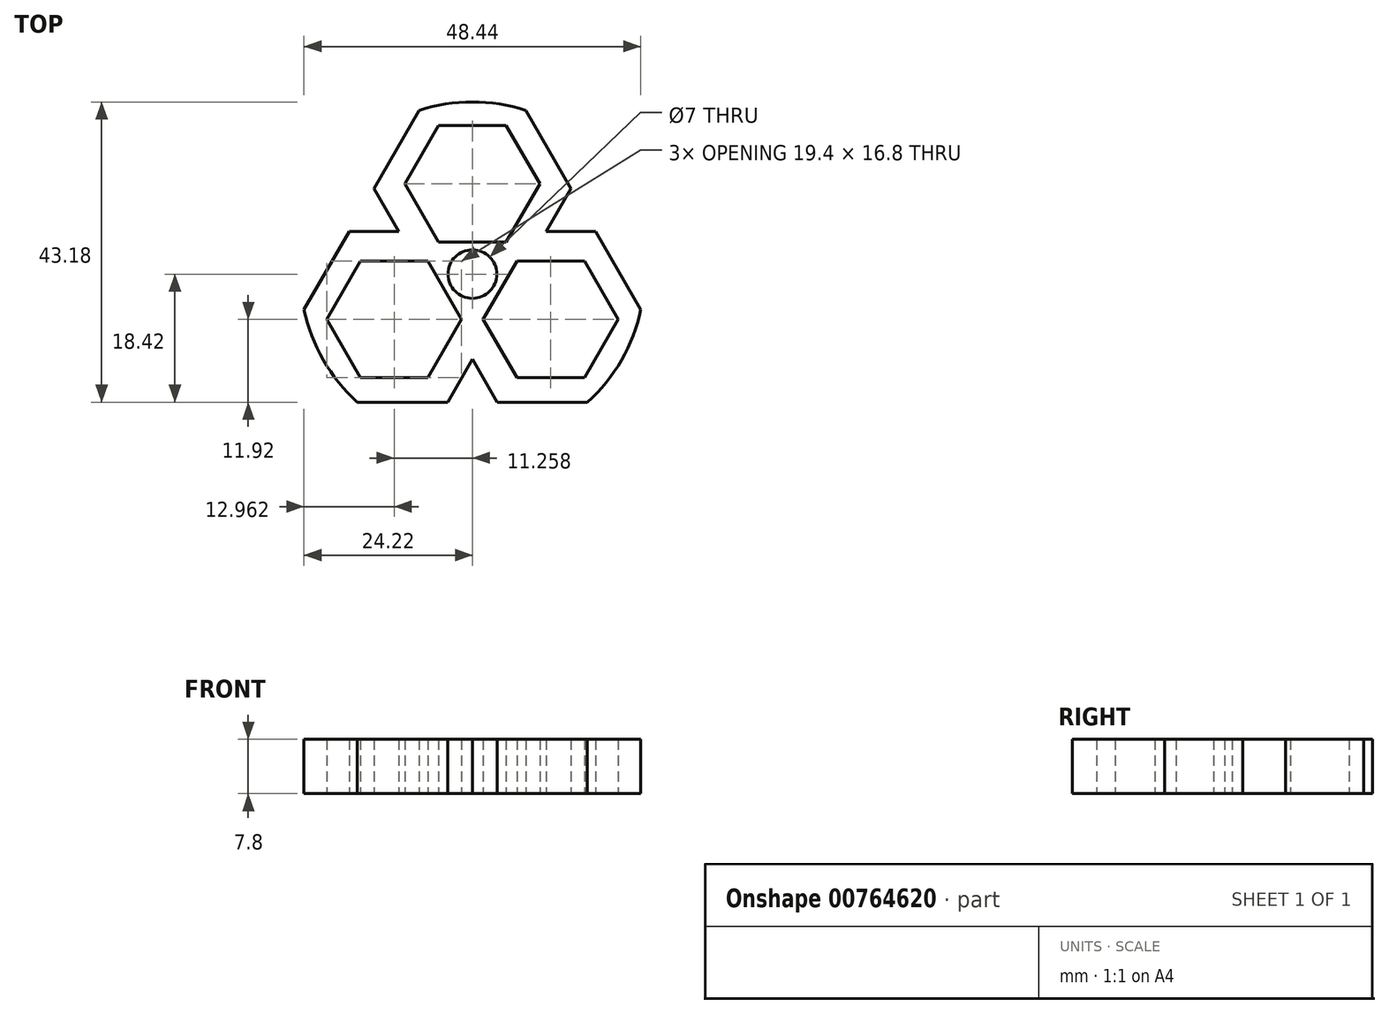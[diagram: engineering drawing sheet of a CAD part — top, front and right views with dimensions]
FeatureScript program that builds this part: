
annotation { "Feature Type Name" : "Feature", "Feature Type Description" : "" }
export const myFeature = defineFeature(function(context is Context, id is Id, definition is map)
    precondition{}
    {
        {
            var Q0;
            Q0=qCreatedBy(makeId("Top.planeOp"),FACE);
            var sketch = newSketch(context, id + "F0", { "sketchPlane" : qUnion([Q0])});
            skCircle(sketch, "E0.cCircle", {"center": v(0, 13) * mm, "radius": 8.4 * mm, "construction": true});
            skLineSegment(sketch, "E0.0", {"start": v(4.85, 4.6) * mm, "end": v(-4.85, 4.6) * mm});
            skLineSegment(sketch, "E0.1", {"start": v(-4.85, 4.6) * mm, "end": v(-9.7, 13) * mm});
            skLineSegment(sketch, "E0.2", {"start": v(-9.7, 13) * mm, "end": v(-4.85, 21.4) * mm});
            skLineSegment(sketch, "E0.3", {"start": v(-4.85, 21.4) * mm, "end": v(4.85, 21.4) * mm});
            skLineSegment(sketch, "E0.4", {"start": v(4.85, 21.4) * mm, "end": v(9.7, 13) * mm});
            skLineSegment(sketch, "E0.5", {"start": v(9.7, 13) * mm, "end": v(4.85, 4.6) * mm});
            skPoint(sketch, "E0.0.midPoint", {"position": v(0, 4.6) * mm});
            skCircle(sketch, "E1", {"center": v(0, 0) * mm, "radius": 3.5 * mm});
            skCircle(sketch, "E2", {"center": v(0, 0) * mm, "radius": 24.76 * mm});
            skLineSegment(sketch, "E3.1.0", {"start": v(-16.1, -14.9) * mm, "end": v(-20.96, -6.5) * mm});
            skLineSegment(sketch, "E3.1.1", {"start": v(-1.56, -6.5) * mm, "end": v(-6.4, -14.9) * mm});
            skLineSegment(sketch, "E3.1.2", {"start": v(-6.4, -14.9) * mm, "end": v(-16.1, -14.9) * mm});
            skLineSegment(sketch, "E3.1.3", {"start": v(-6.4, 1.9) * mm, "end": v(-1.56, -6.5) * mm});
            skLineSegment(sketch, "E3.1.4", {"start": v(-16.1, 1.9) * mm, "end": v(-6.4, 1.9) * mm});
            skLineSegment(sketch, "E3.1.5", {"start": v(-20.96, -6.5) * mm, "end": v(-16.1, 1.9) * mm});
            skLineSegment(sketch, "E3.2.0", {"start": v(20.96, -6.5) * mm, "end": v(16.1, -14.9) * mm});
            skLineSegment(sketch, "E3.2.1", {"start": v(6.4, 1.9) * mm, "end": v(16.1, 1.9) * mm});
            skLineSegment(sketch, "E3.2.2", {"start": v(16.1, 1.9) * mm, "end": v(20.96, -6.5) * mm});
            skLineSegment(sketch, "E3.2.3", {"start": v(1.56, -6.5) * mm, "end": v(6.4, 1.9) * mm});
            skLineSegment(sketch, "E3.2.4", {"start": v(6.4, -14.9) * mm, "end": v(1.56, -6.5) * mm});
            skLineSegment(sketch, "E3.2.5", {"start": v(16.1, -14.9) * mm, "end": v(6.4, -14.9) * mm});
            skPoint(sketch, "E4.0.internal.snap0", {"position": v(3.98, -10.7) * mm});
            skLineSegment(sketch, "E5", {"start": v(0, -12.25) * mm, "end": v(-12.13, -33.25) * mm});
            skLineSegment(sketch, "E6", {"start": v(0, -12.25) * mm, "end": v(12.13, -33.25) * mm});
            skLineSegment(sketch, "E7", {"start": v(12.13, -33.25) * mm, "end": v(-12.13, -33.25) * mm});
            skLineSegment(sketch, "E8.1.0", {"start": v(10.6, 6.12) * mm, "end": v(34.86, 6.12) * mm});
            skLineSegment(sketch, "E8.1.1", {"start": v(10.6, 6.12) * mm, "end": v(22.73, 27.13) * mm});
            skLineSegment(sketch, "E8.1.2", {"start": v(22.73, 27.13) * mm, "end": v(34.86, 6.12) * mm});
            skLineSegment(sketch, "E8.2.0", {"start": v(-10.6, 6.12) * mm, "end": v(-22.73, 27.13) * mm});
            skLineSegment(sketch, "E8.2.1", {"start": v(-10.6, 6.12) * mm, "end": v(-34.86, 6.12) * mm});
            skLineSegment(sketch, "E8.2.2", {"start": v(-34.86, 6.12) * mm, "end": v(-22.73, 27.13) * mm});
            skLineSegment(sketch, "E9", {"start": v(-27.97, -18.42) * mm, "end": v(29.55, -18.42) * mm});
            skLineSegment(sketch, "E10.1.0", {"start": v(29.94, -15.02) * mm, "end": v(1.18, 34.8) * mm});
            skLineSegment(sketch, "E10.2.0", {"start": v(-1.96, 33.43) * mm, "end": v(-30.72, -16.38) * mm});
            skSolve(sketch);
        }
        {
            var Q0;
            Q0=makeQuery(id+"F0.imprint","IMPRINT",FACE,{"disambiguationData":[TD([[makeQuery(id+"F0.imprint","IMPRINT",EDGE,{"derivedFrom":sQuery(id+"F0.wireOp",EDGE,"E0.0")}),1.0]])]});
            extrude(context, id + "F1", {"entities" : qUnion([Q0]), "depth" : 7.8 * mm, "offsetDistance" : 25 * mm});
        }
        {
            var Q0;
            Q0=sQuery(id+"F0.wireOp",EDGE,"E1");
            extrude(context, id + "F2", {"bodyType" : ToolBodyType.SURFACE, "surfaceEntities" : qUnion([Q0]), "depth" : 15 * mm, "offsetDistance" : 25 * mm, "hasSecondDirection" : true, "secondDirectionOppositeDirection" : true, "secondDirectionDepth" : 7.5 * mm});
        }
    });
